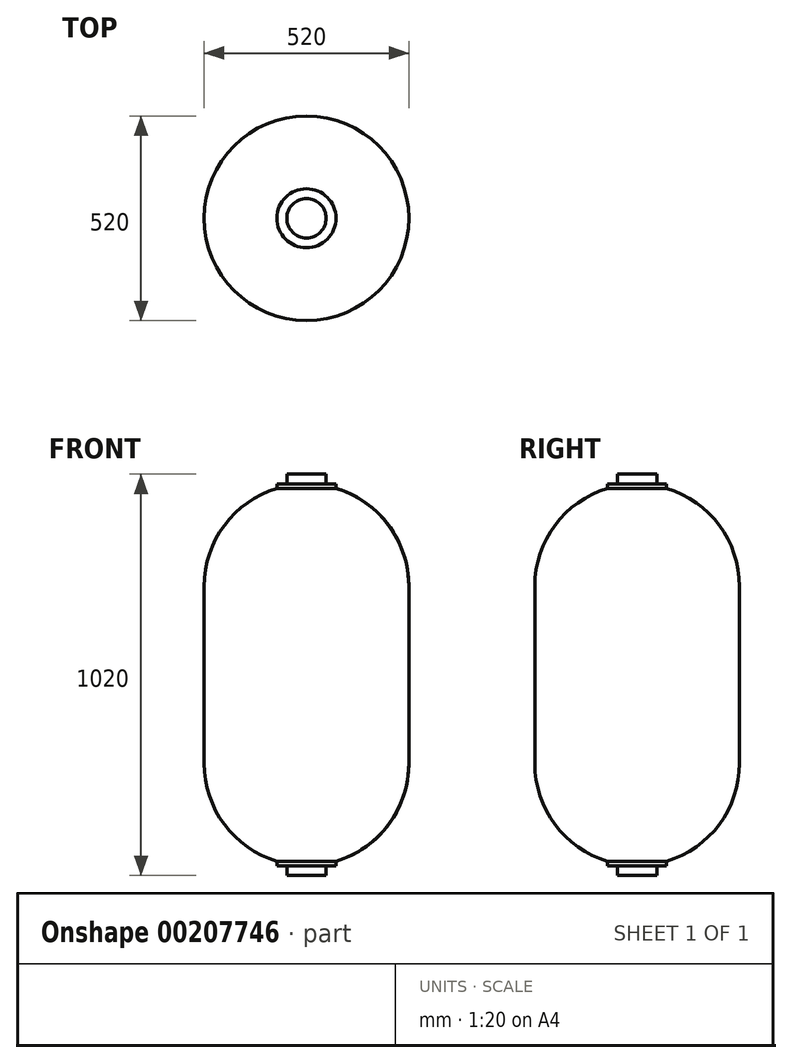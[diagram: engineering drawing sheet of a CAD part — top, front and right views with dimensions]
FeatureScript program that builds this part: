
annotation { "Feature Type Name" : "Feature", "Feature Type Description" : "" }
export const myFeature = defineFeature(function(context is Context, id is Id, definition is map)
    precondition{}
    {
        {
            var Q0;
            Q0=qCreatedBy(makeId("Front.planeOp"),FACE);
            var sketch = newSketch(context, id + "F0", { "sketchPlane" : qUnion([Q0])});
            skArc(sketch, "E0", {"start": v(75, 11.05) * mm, "mid": v(208.69, 104.92) * mm, "end": v(260, 260) * mm});
            skLineSegment(sketch, "E1", {"start": v(260, 260) * mm, "end": v(260, 710) * mm});
            skArc(sketch, "E2", {"start": v(260, 710) * mm, "mid": v(208.69, 865.08) * mm, "end": v(75, 958.95) * mm});
            skLineSegment(sketch, "E3", {"start": v(0, 970) * mm, "end": v(0, 0) * mm});
            skLineSegment(sketch, "E4", {"start": v(75, 11.05) * mm, "end": v(75, 0) * mm});
            skLineSegment(sketch, "E5", {"start": v(75, 0) * mm, "end": v(50, 0) * mm});
            skLineSegment(sketch, "E6", {"start": v(50, 0) * mm, "end": v(50, -25) * mm});
            skLineSegment(sketch, "E7", {"start": v(50, -25) * mm, "end": v(0, -25) * mm});
            skLineSegment(sketch, "E8", {"start": v(0, -25) * mm, "end": v(0, 0) * mm});
            skLineSegment(sketch, "E9", {"start": v(75, 958.95) * mm, "end": v(75, 970) * mm});
            skLineSegment(sketch, "E10", {"start": v(75, 970) * mm, "end": v(50, 970) * mm});
            skLineSegment(sketch, "E11", {"start": v(50, 970) * mm, "end": v(50, 995) * mm});
            skLineSegment(sketch, "E12", {"start": v(50, 995) * mm, "end": v(0, 995) * mm});
            skLineSegment(sketch, "E13", {"start": v(0, 995) * mm, "end": v(0, 970) * mm});
            skSolve(sketch);
        }
        {
            var Q0;
            Q0=makeQuery(id+"F0.imprint","IMPRINT",FACE,{"disambiguationData":[TD([[makeQuery(id+"F0.imprint","IMPRINT",EDGE,{"derivedFrom":sQuery(id+"F0.wireOp",EDGE,"E0")}),1.0]])]});
            var Q1;
            Q1=sQuery(id+"F0.wireOp",EDGE,"E3");
            revolve(context, id + "F1", {"entities" : qUnion([Q0]), "axis" : qUnion([Q1]), "revolveType" : RevolveType.FULL});
        }
    });
